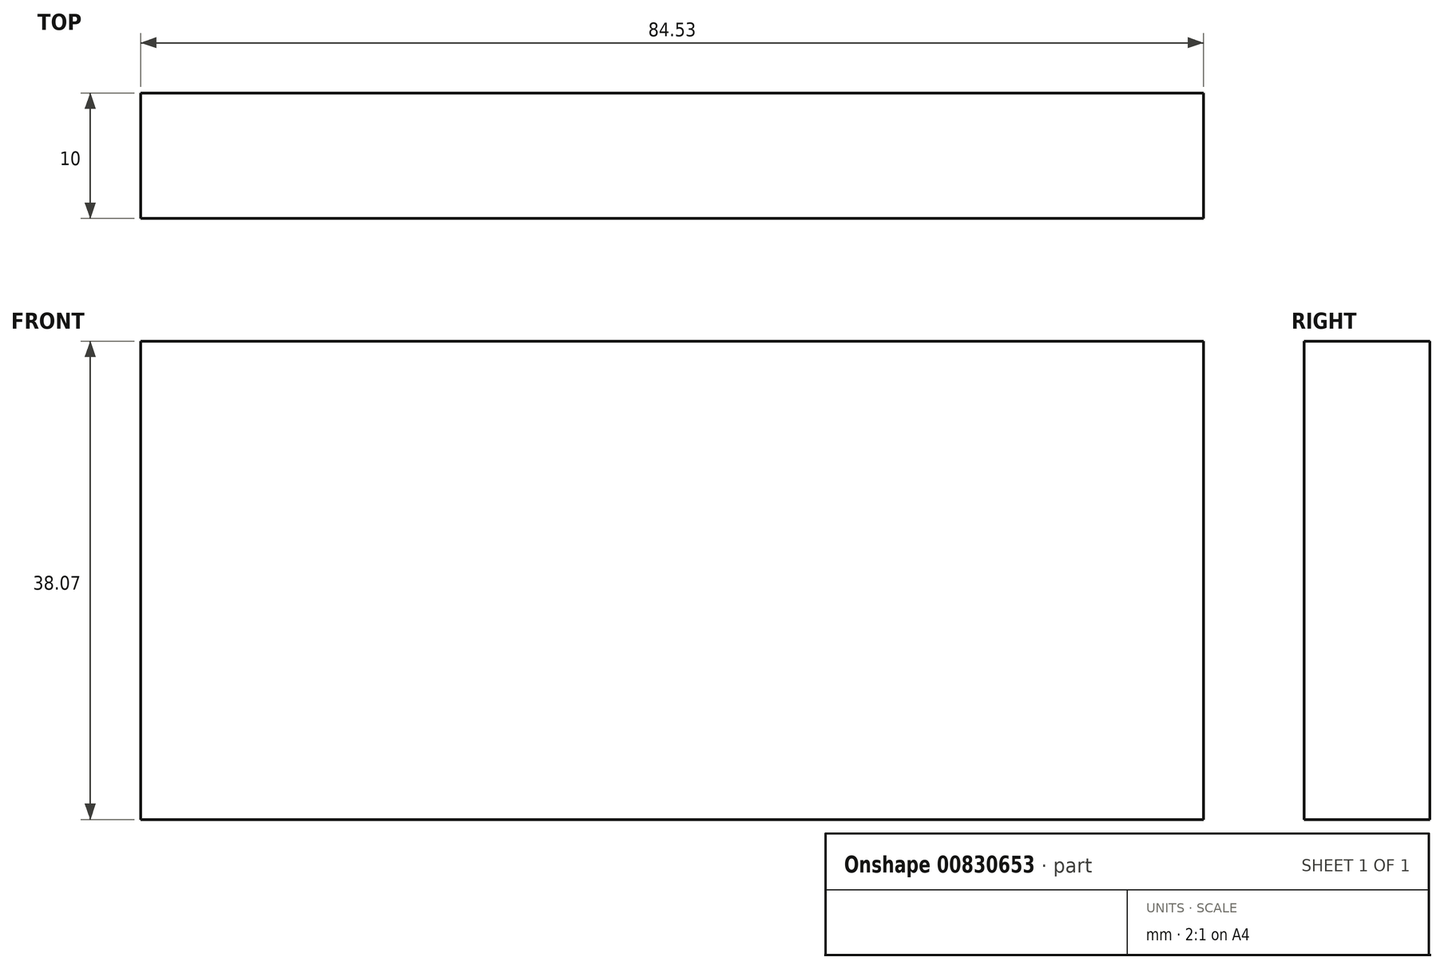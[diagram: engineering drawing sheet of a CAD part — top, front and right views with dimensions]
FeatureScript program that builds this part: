
annotation { "Feature Type Name" : "Feature", "Feature Type Description" : "" }
export const myFeature = defineFeature(function(context is Context, id is Id, definition is map)
    precondition{}
    {
        {
            var Q0;
            Q0=qCreatedBy(makeId("Front.planeOp"),FACE);
            var sketch = newSketch(context, id + "F0", { "sketchPlane" : qUnion([Q0])});
            skLineSegment(sketch, "E0.bottom", {"start": v(0, 0) * mm, "end": v(84.53, 0) * mm});
            skLineSegment(sketch, "E0.top", {"start": v(0, 38.07) * mm, "end": v(84.53, 38.07) * mm});
            skLineSegment(sketch, "E0.left", {"start": v(0, 0) * mm, "end": v(0, 38.07) * mm});
            skLineSegment(sketch, "E0.right", {"start": v(84.53, 0) * mm, "end": v(84.53, 38.07) * mm});
            skSolve(sketch);
        }
        {
            var Q0;
            Q0=makeQuery(id+"F0.imprint","IMPRINT",FACE,{"disambiguationData":[TD([[makeQuery(id+"F0.imprint","IMPRINT",EDGE,{"derivedFrom":sQuery(id+"F0.wireOp",EDGE,"E0.bottom")}),1.0]])]});
            extrude(context, id + "F1", {"entities" : qUnion([Q0]), "depth" : 10 * mm, "offsetDistance" : 25.4 * mm});
        }
    });
